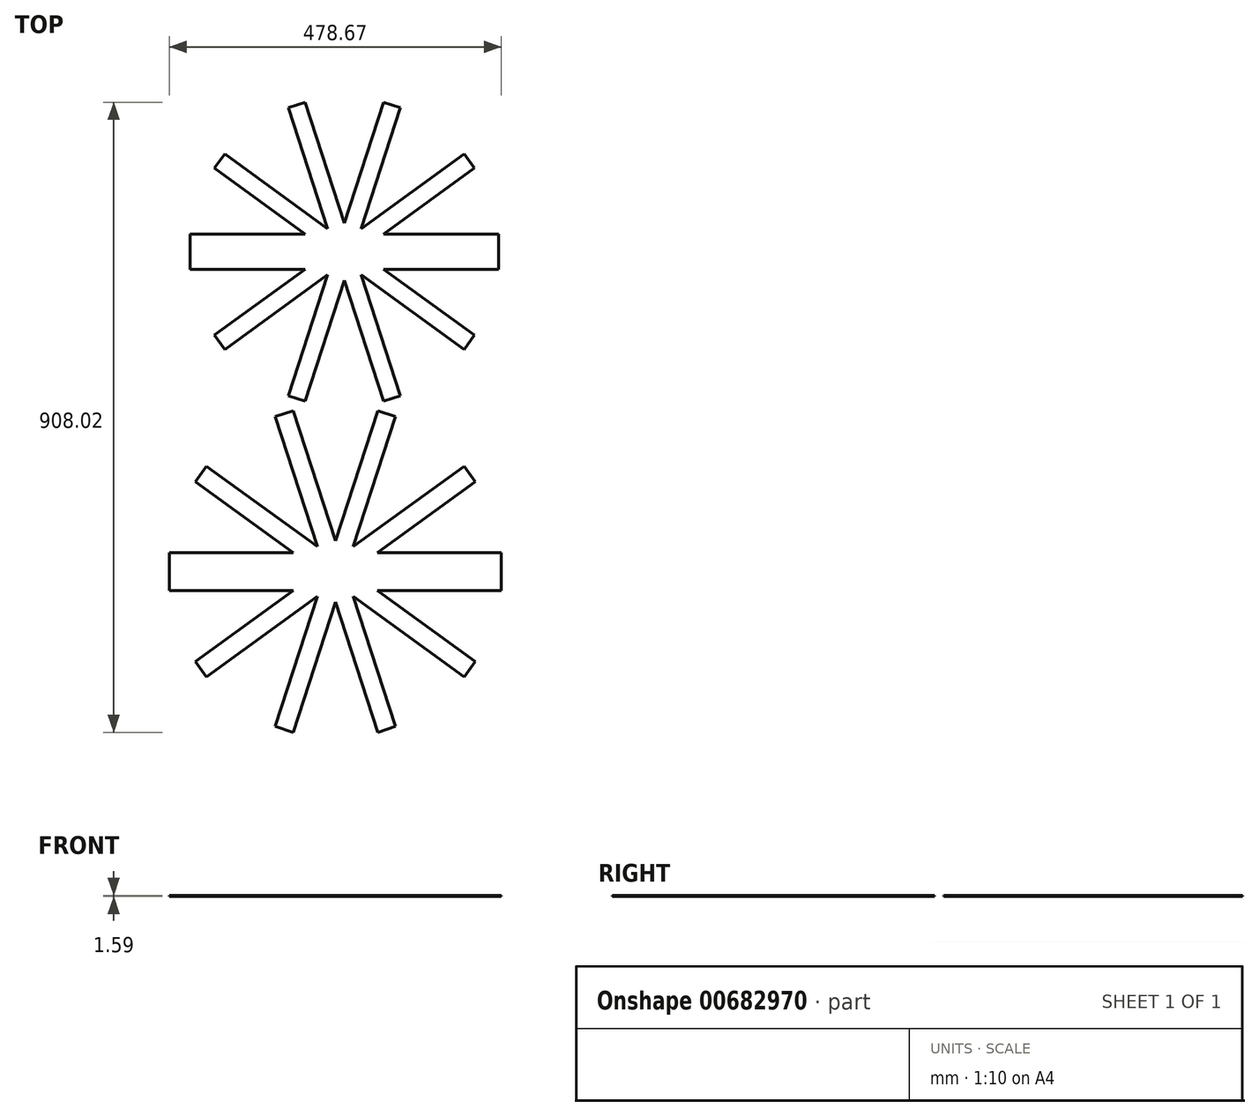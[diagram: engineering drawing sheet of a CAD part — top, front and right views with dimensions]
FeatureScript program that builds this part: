
annotation { "Feature Type Name" : "Feature", "Feature Type Description" : "" }
export const myFeature = defineFeature(function(context is Context, id is Id, definition is map)
    precondition{}
    {
        {
            var Q0;
            Q0=qCreatedBy(makeId("Top.planeOp"),FACE);
            var sketch = newSketch(context, id + "F0", { "sketchPlane" : qUnion([Q0])});
            skLineSegment(sketch, "E0", {"start": v(-2978.88, -2185.65) * mm, "end": v(-1759.68, -2185.65) * mm});
            skLineSegment(sketch, "E1", {"start": v(-1759.68, -2185.65) * mm, "end": v(-1759.68, -966.45) * mm});
            skLineSegment(sketch, "E2", {"start": v(-1759.68, -966.45) * mm, "end": v(-2978.88, -966.45) * mm});
            skLineSegment(sketch, "E3", {"start": v(-2978.88, -966.45) * mm, "end": v(-2978.88, -2185.65) * mm});
            skCircle(sketch, "E4", {"center": v(-1816.57, -1818.69) * mm, "radius": 3.18 * mm});
            skCircle(sketch, "E5", {"center": v(-1816.57, -1837.74) * mm, "radius": 3.18 * mm});
            skCircle(sketch, "E6", {"center": v(-1816.57, -1856.79) * mm, "radius": 3.18 * mm});
            skCircle(sketch, "E7", {"center": v(-1816.57, -1875.84) * mm, "radius": 3.18 * mm});
            skCircle(sketch, "E8", {"center": v(-1816.57, -1894.89) * mm, "radius": 3.18 * mm});
            skArc(sketch, "E9", {"start": v(-2164.46, -1098.62) * mm, "mid": v(-2167.78, -1094.24) * mm, "end": v(-2167.29, -1088.76) * mm});
            skArc(sketch, "E10", {"start": v(-2167.29, -1088.76) * mm, "mid": v(-2109.66, -1019.6) * mm, "end": v(-2026.9, -984.15) * mm});
            skLineSegment(sketch, "E11", {"start": v(-2026.9, -984.15) * mm, "end": v(-1962.06, -984.15) * mm});
            skLineSegment(sketch, "E12", {"start": v(-1962.06, -984.15) * mm, "end": v(-1883.82, -1021.62) * mm});
            skLineSegment(sketch, "E13", {"start": v(-1883.82, -1021.62) * mm, "end": v(-1836.72, -1075.71) * mm});
            skLineSegment(sketch, "E14", {"start": v(-1836.72, -1075.71) * mm, "end": v(-1774.27, -1232.8) * mm});
            skLineSegment(sketch, "E15", {"start": v(-1774.27, -1232.8) * mm, "end": v(-1806.41, -1920.29) * mm});
            skLineSegment(sketch, "E16", {"start": v(-1806.41, -1920.29) * mm, "end": v(-1831.81, -1920.29) * mm});
            skLineSegment(sketch, "E17", {"start": v(-1831.81, -1920.29) * mm, "end": v(-1831.81, -1232.8) * mm});
            skLineSegment(sketch, "E18", {"start": v(-1831.81, -1232.8) * mm, "end": v(-1869.8, -1113.26) * mm});
            skArc(sketch, "E19", {"start": v(-1869.8, -1113.26) * mm, "mid": v(-2010.53, -1004.8) * mm, "end": v(-2159.44, -1101.7) * mm});
            skLineSegment(sketch, "E20", {"start": v(-2159.44, -1101.7) * mm, "end": v(-2164.46, -1098.62) * mm});
            skCircle(sketch, "E21", {"center": v(-1881.26, -1933.81) * mm, "radius": 3.18 * mm});
            skCircle(sketch, "E22", {"center": v(-1881.26, -1952.86) * mm, "radius": 3.18 * mm});
            skCircle(sketch, "E23", {"center": v(-1881.26, -1971.91) * mm, "radius": 3.18 * mm});
            skCircle(sketch, "E24", {"center": v(-1881.26, -1990.96) * mm, "radius": 3.18 * mm});
            skCircle(sketch, "E25", {"center": v(-1881.26, -2010.01) * mm, "radius": 3.18 * mm});
            skArc(sketch, "E26", {"start": v(-2229.15, -1213.74) * mm, "mid": v(-2232.47, -1209.36) * mm, "end": v(-2231.98, -1203.88) * mm});
            skArc(sketch, "E27", {"start": v(-2231.98, -1203.88) * mm, "mid": v(-2174.35, -1134.72) * mm, "end": v(-2091.6, -1099.27) * mm});
            skLineSegment(sketch, "E28", {"start": v(-2091.6, -1099.27) * mm, "end": v(-2026.75, -1099.27) * mm});
            skLineSegment(sketch, "E29", {"start": v(-2026.75, -1099.27) * mm, "end": v(-1948.5, -1136.75) * mm});
            skLineSegment(sketch, "E30", {"start": v(-1948.5, -1136.75) * mm, "end": v(-1901.4, -1190.84) * mm});
            skLineSegment(sketch, "E31", {"start": v(-1901.4, -1190.84) * mm, "end": v(-1838.96, -1347.91) * mm});
            skLineSegment(sketch, "E32", {"start": v(-1838.96, -1347.91) * mm, "end": v(-1871.1, -2035.41) * mm});
            skLineSegment(sketch, "E33", {"start": v(-1871.1, -2035.41) * mm, "end": v(-1896.5, -2035.41) * mm});
            skLineSegment(sketch, "E34", {"start": v(-1896.5, -2035.41) * mm, "end": v(-1896.5, -1347.91) * mm});
            skLineSegment(sketch, "E35", {"start": v(-1896.5, -1347.91) * mm, "end": v(-1934.5, -1228.39) * mm});
            skArc(sketch, "E36", {"start": v(-1934.5, -1228.39) * mm, "mid": v(-2075.22, -1119.91) * mm, "end": v(-2224.13, -1216.83) * mm});
            skLineSegment(sketch, "E37", {"start": v(-2224.13, -1216.83) * mm, "end": v(-2229.15, -1213.74) * mm});
            skCircle(sketch, "E38", {"center": v(-2918, -1823.76) * mm, "radius": 3.18 * mm});
            skCircle(sketch, "E39", {"center": v(-2918, -1842.81) * mm, "radius": 3.18 * mm});
            skCircle(sketch, "E40", {"center": v(-2918, -1861.86) * mm, "radius": 3.18 * mm});
            skCircle(sketch, "E41", {"center": v(-2918, -1880.91) * mm, "radius": 3.18 * mm});
            skCircle(sketch, "E42", {"center": v(-2918, -1899.96) * mm, "radius": 3.18 * mm});
            skArc(sketch, "E43", {"start": v(-2570.1, -1103.7) * mm, "mid": v(-2566.79, -1099.3) * mm, "end": v(-2567.28, -1093.83) * mm});
            skArc(sketch, "E44", {"start": v(-2567.28, -1093.83) * mm, "mid": v(-2624.9, -1024.67) * mm, "end": v(-2707.66, -989.22) * mm});
            skLineSegment(sketch, "E45", {"start": v(-2707.66, -989.22) * mm, "end": v(-2772.5, -989.22) * mm});
            skLineSegment(sketch, "E46", {"start": v(-2772.5, -989.22) * mm, "end": v(-2850.75, -1026.7) * mm});
            skLineSegment(sketch, "E47", {"start": v(-2850.75, -1026.7) * mm, "end": v(-2897.85, -1080.79) * mm});
            skLineSegment(sketch, "E48", {"start": v(-2897.85, -1080.79) * mm, "end": v(-2960.3, -1237.86) * mm});
            skLineSegment(sketch, "E49", {"start": v(-2960.3, -1237.86) * mm, "end": v(-2928.15, -1925.36) * mm});
            skLineSegment(sketch, "E50", {"start": v(-2928.15, -1925.36) * mm, "end": v(-2902.75, -1925.36) * mm});
            skLineSegment(sketch, "E51", {"start": v(-2902.75, -1925.36) * mm, "end": v(-2902.75, -1237.86) * mm});
            skLineSegment(sketch, "E52", {"start": v(-2902.75, -1237.86) * mm, "end": v(-2864.76, -1118.33) * mm});
            skArc(sketch, "E53", {"start": v(-2864.76, -1118.33) * mm, "mid": v(-2724.04, -1009.86) * mm, "end": v(-2575.12, -1106.78) * mm});
            skLineSegment(sketch, "E54", {"start": v(-2575.12, -1106.78) * mm, "end": v(-2570.1, -1103.7) * mm});
            skCircle(sketch, "E55", {"center": v(-2843.86, -1946.06) * mm, "radius": 3.18 * mm});
            skCircle(sketch, "E56", {"center": v(-2843.86, -1965.11) * mm, "radius": 3.18 * mm});
            skCircle(sketch, "E57", {"center": v(-2843.86, -1984.16) * mm, "radius": 3.18 * mm});
            skCircle(sketch, "E58", {"center": v(-2843.86, -2003.21) * mm, "radius": 3.18 * mm});
            skCircle(sketch, "E59", {"center": v(-2843.86, -2022.26) * mm, "radius": 3.18 * mm});
            skArc(sketch, "E60", {"start": v(-2495.97, -1226) * mm, "mid": v(-2492.65, -1221.6) * mm, "end": v(-2493.14, -1216.13) * mm});
            skArc(sketch, "E61", {"start": v(-2493.14, -1216.13) * mm, "mid": v(-2550.77, -1146.97) * mm, "end": v(-2633.52, -1111.52) * mm});
            skLineSegment(sketch, "E62", {"start": v(-2633.52, -1111.52) * mm, "end": v(-2698.37, -1111.52) * mm});
            skLineSegment(sketch, "E63", {"start": v(-2698.37, -1111.52) * mm, "end": v(-2776.62, -1149) * mm});
            skLineSegment(sketch, "E64", {"start": v(-2776.62, -1149) * mm, "end": v(-2823.71, -1203.09) * mm});
            skLineSegment(sketch, "E65", {"start": v(-2823.71, -1203.09) * mm, "end": v(-2886.16, -1360.16) * mm});
            skLineSegment(sketch, "E66", {"start": v(-2886.16, -1360.16) * mm, "end": v(-2854.02, -2047.66) * mm});
            skLineSegment(sketch, "E67", {"start": v(-2854.02, -2047.66) * mm, "end": v(-2828.62, -2047.66) * mm});
            skLineSegment(sketch, "E68", {"start": v(-2828.62, -2047.66) * mm, "end": v(-2828.62, -1360.16) * mm});
            skLineSegment(sketch, "E69", {"start": v(-2828.62, -1360.16) * mm, "end": v(-2790.63, -1240.63) * mm});
            skArc(sketch, "E70", {"start": v(-2790.63, -1240.63) * mm, "mid": v(-2649.9, -1132.16) * mm, "end": v(-2500.99, -1229.08) * mm});
            skLineSegment(sketch, "E71", {"start": v(-2500.99, -1229.08) * mm, "end": v(-2495.97, -1226) * mm});
            skLineSegment(sketch, "E72", {"start": v(-2467.11, -985.4) * mm, "end": v(-2416.4, -988.46) * mm});
            skLineSegment(sketch, "E73", {"start": v(-2416.4, -988.46) * mm, "end": v(-2488.14, -2178.15) * mm});
            skLineSegment(sketch, "E74", {"start": v(-2488.14, -2178.15) * mm, "end": v(-2538.85, -2175.1) * mm});
            skLineSegment(sketch, "E75", {"start": v(-2538.85, -2175.1) * mm, "end": v(-2467.11, -985.4) * mm});
            skLineSegment(sketch, "E76", {"start": v(-2450.35, -1050.35) * mm, "end": v(-2448.79, -1024.36) * mm});
            skArc(sketch, "E77", {"start": v(-2448.79, -1024.36) * mm, "mid": v(-2443.75, -1019.9) * mm, "end": v(-2439.28, -1024.93) * mm});
            skLineSegment(sketch, "E78", {"start": v(-2439.28, -1024.93) * mm, "end": v(-2440.85, -1050.92) * mm});
            skArc(sketch, "E79", {"start": v(-2440.85, -1050.92) * mm, "mid": v(-2445.89, -1055.39) * mm, "end": v(-2450.35, -1050.35) * mm});
            skLineSegment(sketch, "E80", {"start": v(-2466.02, -1310.22) * mm, "end": v(-2464.46, -1284.24) * mm});
            skArc(sketch, "E81", {"start": v(-2464.46, -1284.24) * mm, "mid": v(-2459.42, -1279.77) * mm, "end": v(-2454.95, -1284.81) * mm});
            skLineSegment(sketch, "E82", {"start": v(-2454.95, -1284.81) * mm, "end": v(-2456.52, -1310.8) * mm});
            skArc(sketch, "E83", {"start": v(-2456.52, -1310.8) * mm, "mid": v(-2461.56, -1315.27) * mm, "end": v(-2466.02, -1310.22) * mm});
            skLineSegment(sketch, "E84", {"start": v(-2396.67, -989.65) * mm, "end": v(-2345.97, -992.7) * mm});
            skLineSegment(sketch, "E85", {"start": v(-2345.97, -992.7) * mm, "end": v(-2417.7, -2182.4) * mm});
            skLineSegment(sketch, "E86", {"start": v(-2417.7, -2182.4) * mm, "end": v(-2468.4, -2179.34) * mm});
            skLineSegment(sketch, "E87", {"start": v(-2468.4, -2179.34) * mm, "end": v(-2396.67, -989.65) * mm});
            skLineSegment(sketch, "E88", {"start": v(-2379.92, -1054.6) * mm, "end": v(-2378.35, -1028.6) * mm});
            skArc(sketch, "E89", {"start": v(-2378.35, -1028.6) * mm, "mid": v(-2373.3, -1024.14) * mm, "end": v(-2368.84, -1029.18) * mm});
            skLineSegment(sketch, "E90", {"start": v(-2368.84, -1029.18) * mm, "end": v(-2370.4, -1055.17) * mm});
            skArc(sketch, "E91", {"start": v(-2370.4, -1055.17) * mm, "mid": v(-2375.45, -1059.63) * mm, "end": v(-2379.92, -1054.6) * mm});
            skLineSegment(sketch, "E92", {"start": v(-2395.59, -1314.47) * mm, "end": v(-2394.02, -1288.48) * mm});
            skArc(sketch, "E93", {"start": v(-2394.02, -1288.48) * mm, "mid": v(-2388.98, -1284.02) * mm, "end": v(-2384.51, -1289.06) * mm});
            skLineSegment(sketch, "E94", {"start": v(-2384.51, -1289.06) * mm, "end": v(-2386.08, -1315.05) * mm});
            skArc(sketch, "E95", {"start": v(-2386.08, -1315.05) * mm, "mid": v(-2391.12, -1319.51) * mm, "end": v(-2395.59, -1314.47) * mm});
            skLineSegment(sketch, "E96", {"start": v(-2106.73, -1425.28) * mm, "end": v(-2050.13, -1251.1) * mm});
            skLineSegment(sketch, "E97", {"start": v(-2050.13, -1251.1) * mm, "end": v(-2074.29, -1243.24) * mm});
            skLineSegment(sketch, "E98", {"start": v(-2074.29, -1243.24) * mm, "end": v(-2130.88, -1417.43) * mm});
            skLineSegment(sketch, "E99", {"start": v(-2130.88, -1417.43) * mm, "end": v(-2187.48, -1243.24) * mm});
            skLineSegment(sketch, "E100", {"start": v(-2187.48, -1243.24) * mm, "end": v(-2211.64, -1251.1) * mm});
            skLineSegment(sketch, "E101", {"start": v(-2211.64, -1251.1) * mm, "end": v(-2155.04, -1425.28) * mm});
            skLineSegment(sketch, "E102", {"start": v(-2155.04, -1425.28) * mm, "end": v(-2303.21, -1317.62) * mm});
            skLineSegment(sketch, "E103", {"start": v(-2303.21, -1317.62) * mm, "end": v(-2318.14, -1338.17) * mm});
            skLineSegment(sketch, "E104", {"start": v(-2318.14, -1338.17) * mm, "end": v(-2187.45, -1433.13) * mm});
            skLineSegment(sketch, "E105", {"start": v(-2187.45, -1433.13) * mm, "end": v(-2353.12, -1433.13) * mm});
            skLineSegment(sketch, "E106", {"start": v(-2353.12, -1433.13) * mm, "end": v(-2353.12, -1458.53) * mm});
            skLineSegment(sketch, "E107", {"start": v(-2353.12, -1458.53) * mm, "end": v(-2353.12, -1483.93) * mm});
            skLineSegment(sketch, "E108", {"start": v(-2353.12, -1483.93) * mm, "end": v(-2187.45, -1483.93) * mm});
            skLineSegment(sketch, "E109", {"start": v(-2187.45, -1483.93) * mm, "end": v(-2318.14, -1578.88) * mm});
            skLineSegment(sketch, "E110", {"start": v(-2318.14, -1578.88) * mm, "end": v(-2303.21, -1599.43) * mm});
            skLineSegment(sketch, "E111", {"start": v(-2303.21, -1599.43) * mm, "end": v(-2155.04, -1491.78) * mm});
            skLineSegment(sketch, "E112", {"start": v(-2155.04, -1491.78) * mm, "end": v(-2211.64, -1665.96) * mm});
            skLineSegment(sketch, "E113", {"start": v(-2211.64, -1665.96) * mm, "end": v(-2187.48, -1673.81) * mm});
            skLineSegment(sketch, "E114", {"start": v(-2187.48, -1673.81) * mm, "end": v(-2130.88, -1499.62) * mm});
            skLineSegment(sketch, "E115", {"start": v(-2130.88, -1499.62) * mm, "end": v(-2074.29, -1673.81) * mm});
            skLineSegment(sketch, "E116", {"start": v(-2074.29, -1673.81) * mm, "end": v(-2050.13, -1665.96) * mm});
            skLineSegment(sketch, "E117", {"start": v(-2050.13, -1665.96) * mm, "end": v(-2106.73, -1491.78) * mm});
            skLineSegment(sketch, "E118", {"start": v(-2106.73, -1491.78) * mm, "end": v(-1958.56, -1599.43) * mm});
            skLineSegment(sketch, "E119", {"start": v(-1958.56, -1599.43) * mm, "end": v(-1943.63, -1578.88) * mm});
            skLineSegment(sketch, "E120", {"start": v(-1943.63, -1578.88) * mm, "end": v(-2074.32, -1483.93) * mm});
            skLineSegment(sketch, "E121", {"start": v(-2074.32, -1483.93) * mm, "end": v(-1908.65, -1483.93) * mm});
            skLineSegment(sketch, "E122", {"start": v(-1908.65, -1483.93) * mm, "end": v(-1908.65, -1458.53) * mm});
            skLineSegment(sketch, "E123", {"start": v(-1908.65, -1458.53) * mm, "end": v(-1908.65, -1433.13) * mm});
            skLineSegment(sketch, "E124", {"start": v(-1908.65, -1433.13) * mm, "end": v(-2074.32, -1433.13) * mm});
            skLineSegment(sketch, "E125", {"start": v(-2074.32, -1433.13) * mm, "end": v(-1943.63, -1338.17) * mm});
            skLineSegment(sketch, "E126", {"start": v(-1943.63, -1338.17) * mm, "end": v(-1958.56, -1317.62) * mm});
            skLineSegment(sketch, "E127", {"start": v(-1958.56, -1317.62) * mm, "end": v(-2106.73, -1425.28) * mm});
            skLineSegment(sketch, "E128", {"start": v(-2118.05, -1883.61) * mm, "end": v(-2057.1, -1696.03) * mm});
            skLineSegment(sketch, "E129", {"start": v(-2057.1, -1696.03) * mm, "end": v(-2083.11, -1687.57) * mm});
            skLineSegment(sketch, "E130", {"start": v(-2083.11, -1687.57) * mm, "end": v(-2144.06, -1875.16) * mm});
            skLineSegment(sketch, "E131", {"start": v(-2144.06, -1875.16) * mm, "end": v(-2205.01, -1687.57) * mm});
            skLineSegment(sketch, "E132", {"start": v(-2205.01, -1687.57) * mm, "end": v(-2231.03, -1696.03) * mm});
            skLineSegment(sketch, "E133", {"start": v(-2231.03, -1696.03) * mm, "end": v(-2170.08, -1883.61) * mm});
            skLineSegment(sketch, "E134", {"start": v(-2170.08, -1883.61) * mm, "end": v(-2329.65, -1767.68) * mm});
            skLineSegment(sketch, "E135", {"start": v(-2329.65, -1767.68) * mm, "end": v(-2345.73, -1789.8) * mm});
            skLineSegment(sketch, "E136", {"start": v(-2345.73, -1789.8) * mm, "end": v(-2204.98, -1892.06) * mm});
            skLineSegment(sketch, "E137", {"start": v(-2204.98, -1892.06) * mm, "end": v(-2383.4, -1892.06) * mm});
            skLineSegment(sketch, "E138", {"start": v(-2383.4, -1892.06) * mm, "end": v(-2383.4, -1919.42) * mm});
            skLineSegment(sketch, "E139", {"start": v(-2383.4, -1919.42) * mm, "end": v(-2383.4, -1946.77) * mm});
            skLineSegment(sketch, "E140", {"start": v(-2383.4, -1946.77) * mm, "end": v(-2204.98, -1946.77) * mm});
            skLineSegment(sketch, "E141", {"start": v(-2204.98, -1946.77) * mm, "end": v(-2345.73, -2049.03) * mm});
            skLineSegment(sketch, "E142", {"start": v(-2345.73, -2049.03) * mm, "end": v(-2329.65, -2071.16) * mm});
            skLineSegment(sketch, "E143", {"start": v(-2329.65, -2071.16) * mm, "end": v(-2170.08, -1955.22) * mm});
            skLineSegment(sketch, "E144", {"start": v(-2170.08, -1955.22) * mm, "end": v(-2231.03, -2142.8) * mm});
            skLineSegment(sketch, "E145", {"start": v(-2231.03, -2142.8) * mm, "end": v(-2205.01, -2151.26) * mm});
            skLineSegment(sketch, "E146", {"start": v(-2205.01, -2151.26) * mm, "end": v(-2144.06, -1963.68) * mm});
            skLineSegment(sketch, "E147", {"start": v(-2144.06, -1963.68) * mm, "end": v(-2083.11, -2151.26) * mm});
            skLineSegment(sketch, "E148", {"start": v(-2083.11, -2151.26) * mm, "end": v(-2057.1, -2142.8) * mm});
            skLineSegment(sketch, "E149", {"start": v(-2057.1, -2142.8) * mm, "end": v(-2118.05, -1955.22) * mm});
            skLineSegment(sketch, "E150", {"start": v(-2118.05, -1955.22) * mm, "end": v(-1958.48, -2071.16) * mm});
            skLineSegment(sketch, "E151", {"start": v(-1958.48, -2071.16) * mm, "end": v(-1942.4, -2049.03) * mm});
            skLineSegment(sketch, "E152", {"start": v(-1942.4, -2049.03) * mm, "end": v(-2083.14, -1946.77) * mm});
            skLineSegment(sketch, "E153", {"start": v(-2083.14, -1946.77) * mm, "end": v(-1904.73, -1946.77) * mm});
            skLineSegment(sketch, "E154", {"start": v(-1904.73, -1946.77) * mm, "end": v(-1904.73, -1919.42) * mm});
            skLineSegment(sketch, "E155", {"start": v(-1904.73, -1919.42) * mm, "end": v(-1904.73, -1892.06) * mm});
            skLineSegment(sketch, "E156", {"start": v(-1904.73, -1892.06) * mm, "end": v(-2083.14, -1892.06) * mm});
            skLineSegment(sketch, "E157", {"start": v(-2083.14, -1892.06) * mm, "end": v(-1942.4, -1789.8) * mm});
            skLineSegment(sketch, "E158", {"start": v(-1942.4, -1789.8) * mm, "end": v(-1958.48, -1767.68) * mm});
            skLineSegment(sketch, "E159", {"start": v(-1958.48, -1767.68) * mm, "end": v(-2118.05, -1883.61) * mm});
            skLineSegment(sketch, "E160", {"start": v(-2779.2, -2157.89) * mm, "end": v(-2705.12, -1203.2) * mm});
            skLineSegment(sketch, "E161", {"start": v(-2705.12, -1203.2) * mm, "end": v(-2730.44, -1201.24) * mm});
            skLineSegment(sketch, "E162", {"start": v(-2730.44, -1201.24) * mm, "end": v(-2804.52, -2155.92) * mm});
            skLineSegment(sketch, "E163", {"start": v(-2804.52, -2155.92) * mm, "end": v(-2779.2, -2157.89) * mm});
            skLineSegment(sketch, "E164", {"start": v(-2730.55, -2177.66) * mm, "end": v(-2657.84, -1149.02) * mm});
            skLineSegment(sketch, "E165", {"start": v(-2657.84, -1149.02) * mm, "end": v(-2683.18, -1147.22) * mm});
            skLineSegment(sketch, "E166", {"start": v(-2683.18, -1147.22) * mm, "end": v(-2755.9, -2175.87) * mm});
            skLineSegment(sketch, "E167", {"start": v(-2755.9, -2175.87) * mm, "end": v(-2730.55, -2177.66) * mm});
            skSolve(sketch);
        }
        {
            var Q0;
            Q0=makeQuery(id+"F0.imprint","IMPRINT",FACE,{"disambiguationData":[TD([[makeQuery(id+"F0.imprint","IMPRINT",EDGE,{"derivedFrom":sQuery(id+"F0.wireOp",EDGE,"E96")}),1.0]])]});
            var Q1;
            Q1=makeQuery(id+"F0.imprint","IMPRINT",FACE,{"disambiguationData":[TD([[makeQuery(id+"F0.imprint","IMPRINT",EDGE,{"derivedFrom":sQuery(id+"F0.wireOp",EDGE,"E128")}),1.0]])]});
            extrude(context, id + "F1", {"entities" : qUnion([Q0, Q1]), "depth" : 1.59 * mm, "offsetDistance" : 25.4 * mm});
        }
    });
